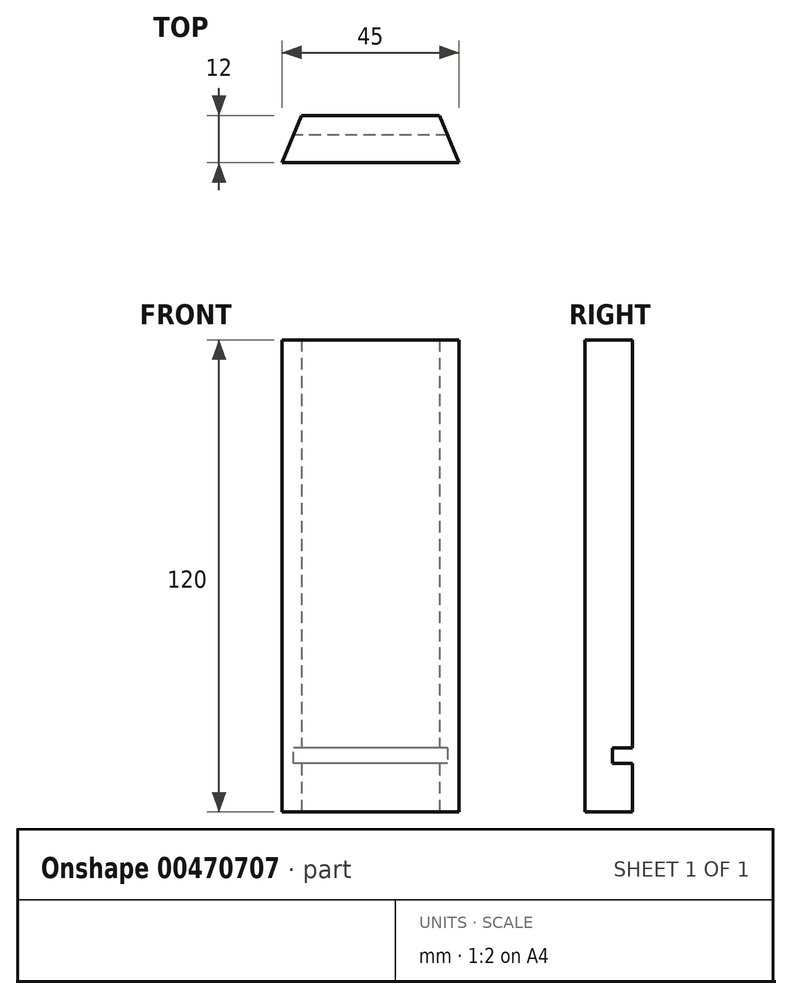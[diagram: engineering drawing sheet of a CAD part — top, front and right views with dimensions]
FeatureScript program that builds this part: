
annotation { "Feature Type Name" : "Feature", "Feature Type Description" : "" }
export const myFeature = defineFeature(function(context is Context, id is Id, definition is map)
    precondition{}
    {
        {
            var Q0;
            Q0=qCreatedBy(makeId("Top.planeOp"),FACE);
            var sketch = newSketch(context, id + "F0", { "sketchPlane" : qUnion([Q0])});
            skLineSegment(sketch, "E0.bottom", {"start": v(-18.82, -43.71) * mm, "end": v(26.18, -43.71) * mm});
            skLineSegment(sketch, "E0.top", {"start": v(-18.82, -31.71) * mm, "end": v(26.18, -31.71) * mm});
            skLineSegment(sketch, "E0.left", {"start": v(-18.82, -43.71) * mm, "end": v(-18.82, -31.71) * mm});
            skLineSegment(sketch, "E0.right", {"start": v(26.18, -43.71) * mm, "end": v(26.18, -31.71) * mm});
            skLineSegment(sketch, "E1", {"start": v(-18.82, -43.71) * mm, "end": v(-13.85, -31.71) * mm});
            skLineSegment(sketch, "E2", {"start": v(26.18, -43.71) * mm, "end": v(21.2, -31.71) * mm});
            skSolve(sketch);
        }
        {
            var Q0;
            Q0=makeQuery(id+"F0.imprint","IMPRINT",FACE,{"disambiguationData":[TD([[makeQuery(id+"F0.imprint","IMPRINT",EDGE,{"derivedFrom":sQuery(id+"F0.wireOp",EDGE,"E0.bottom")}),1.0]])]});
            extrude(context, id + "F1", {"entities" : qUnion([Q0]), "depth" : 120 * mm});
        }
        {
            var Q0;
            Q0=makeQuery(id+"F1.opExtrude","SWEPT_FACE",FACE,{"disambiguationData":[OSD([sQuery(id+"F0.wireOp",EDGE,"E0.top")])]});
            var sketch = newSketch(context, id + "F2", { "sketchPlane" : qUnion([Q0])});
            skLineSegment(sketch, "E3.bottom", {"start": v(-21.2, 12.3) * mm, "end": v(13.85, 12.3) * mm});
            skLineSegment(sketch, "E3.top", {"start": v(-21.2, 16.32) * mm, "end": v(13.85, 16.32) * mm});
            skLineSegment(sketch, "E3.left", {"start": v(-21.2, 12.3) * mm, "end": v(-21.2, 16.32) * mm});
            skLineSegment(sketch, "E3.right", {"start": v(13.85, 12.3) * mm, "end": v(13.85, 16.32) * mm});
            skSolve(sketch);
        }
        {
            var Q0;
            Q0=makeQuery(id+"F2.imprint","IMPRINT",FACE,{"disambiguationData":[TD([[makeQuery(id+"F2.imprint","IMPRINT",EDGE,{"derivedFrom":sQuery(id+"F2.wireOp",EDGE,"E3.bottom")}),1.0]])]});
            extrude(context, id + "F3", {"entities" : qUnion([Q0]), "operationType" : NewBodyOperationType.REMOVE, "oppositeDirection" : true, "depth" : 5 * mm});
        }
        {
            var Q0;
            Q0=makeQuery(id+"F3.boolean.opBoolean","COPY",FACE,{"derivedFrom":makeQuery(id+"F3.opExtrude","SWEPT_FACE",FACE,{"disambiguationData":[OSD([sQuery(id+"F2.wireOp",EDGE,"E3.right")])]})});
            var sketch = newSketch(context, id + "F4", { "sketchPlane" : qUnion([Q0])});
            skLineSegment(sketch, "E4.bottom", {"start": v(-36.71, 12.3) * mm, "end": v(-31.71, 12.3) * mm});
            skLineSegment(sketch, "E4.top", {"start": v(-36.71, 16.32) * mm, "end": v(-31.71, 16.32) * mm});
            skLineSegment(sketch, "E4.left", {"start": v(-36.71, 12.3) * mm, "end": v(-36.71, 16.32) * mm});
            skLineSegment(sketch, "E4.right", {"start": v(-31.71, 12.3) * mm, "end": v(-31.71, 16.32) * mm});
            skSolve(sketch);
        }
        {
            var Q0;
            Q0=makeQuery(id+"F4.imprint","IMPRINT",FACE,{"disambiguationData":[TD([[makeQuery(id+"F4.imprint","IMPRINT",EDGE,{"derivedFrom":sQuery(id+"F4.wireOp",EDGE,"E4.bottom")}),1.0]])]});
            extrude(context, id + "F5", {"entities" : qUnion([Q0]), "operationType" : NewBodyOperationType.REMOVE, "oppositeDirection" : true, "depth" : 25 * mm});
        }
        {
            var Q0;
            Q0=makeQuery(id+"F3.boolean.opBoolean","COPY",FACE,{"derivedFrom":makeQuery(id+"F3.opExtrude","SWEPT_FACE",FACE,{"disambiguationData":[OSD([sQuery(id+"F2.wireOp",EDGE,"E3.left")])]})});
            var sketch = newSketch(context, id + "F6", { "sketchPlane" : qUnion([Q0])});
            skLineSegment(sketch, "E5.bottom", {"start": v(31.71, 12.3) * mm, "end": v(36.71, 12.3) * mm});
            skLineSegment(sketch, "E5.top", {"start": v(31.71, 16.32) * mm, "end": v(36.71, 16.32) * mm});
            skLineSegment(sketch, "E5.left", {"start": v(31.71, 12.3) * mm, "end": v(31.71, 16.32) * mm});
            skLineSegment(sketch, "E5.right", {"start": v(36.71, 12.3) * mm, "end": v(36.71, 16.32) * mm});
            skSolve(sketch);
        }
        {
            var Q0;
            Q0=makeQuery(id+"F6.imprint","IMPRINT",FACE,{"disambiguationData":[TD([[makeQuery(id+"F6.imprint","IMPRINT",EDGE,{"derivedFrom":sQuery(id+"F6.wireOp",EDGE,"E5.bottom")}),-1.0]])]});
            extrude(context, id + "F7", {"entities" : qUnion([Q0]), "operationType" : NewBodyOperationType.REMOVE, "oppositeDirection" : true, "depth" : 25 * mm});
        }
    });
